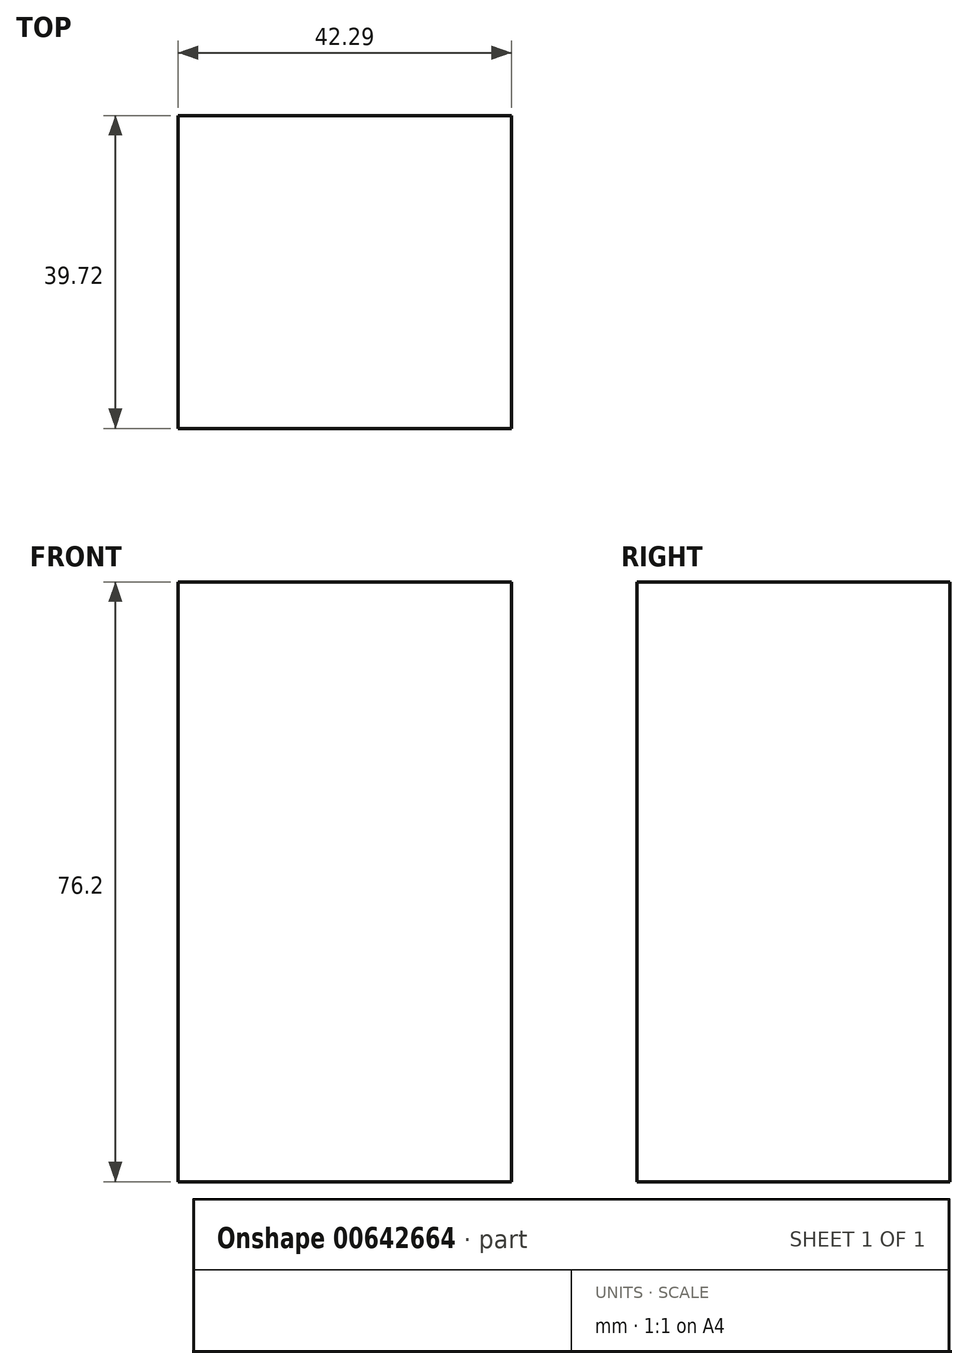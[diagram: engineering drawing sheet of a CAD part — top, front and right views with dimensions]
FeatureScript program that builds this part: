
annotation { "Feature Type Name" : "Feature", "Feature Type Description" : "" }
export const myFeature = defineFeature(function(context is Context, id is Id, definition is map)
    precondition{}
    {
        {
            var Q0;
            Q0=qCreatedBy(makeId("Top.planeOp"),FACE);
            var sketch = newSketch(context, id + "F0", { "sketchPlane" : qUnion([Q0])});
            skLineSegment(sketch, "E0.bottom", {"start": v(0, 0) * mm, "end": v(-42.3, 0) * mm});
            skLineSegment(sketch, "E0.top", {"start": v(0, 39.72) * mm, "end": v(-42.3, 39.72) * mm});
            skLineSegment(sketch, "E0.left", {"start": v(0, 0) * mm, "end": v(0, 39.72) * mm});
            skLineSegment(sketch, "E0.right", {"start": v(-42.3, 0) * mm, "end": v(-42.3, 39.72) * mm});
            skSolve(sketch);
        }
        {
            var Q0;
            Q0=makeQuery(id+"F0.imprint","IMPRINT",FACE,{"disambiguationData":[TD([[makeQuery(id+"F0.imprint","IMPRINT",EDGE,{"derivedFrom":sQuery(id+"F0.wireOp",EDGE,"E0.bottom")}),-1.0]])]});
            extrude(context, id + "F1", {"entities" : qUnion([Q0]), "depth" : 76.2 * mm, "offsetDistance" : 25.4 * mm});
        }
    });
